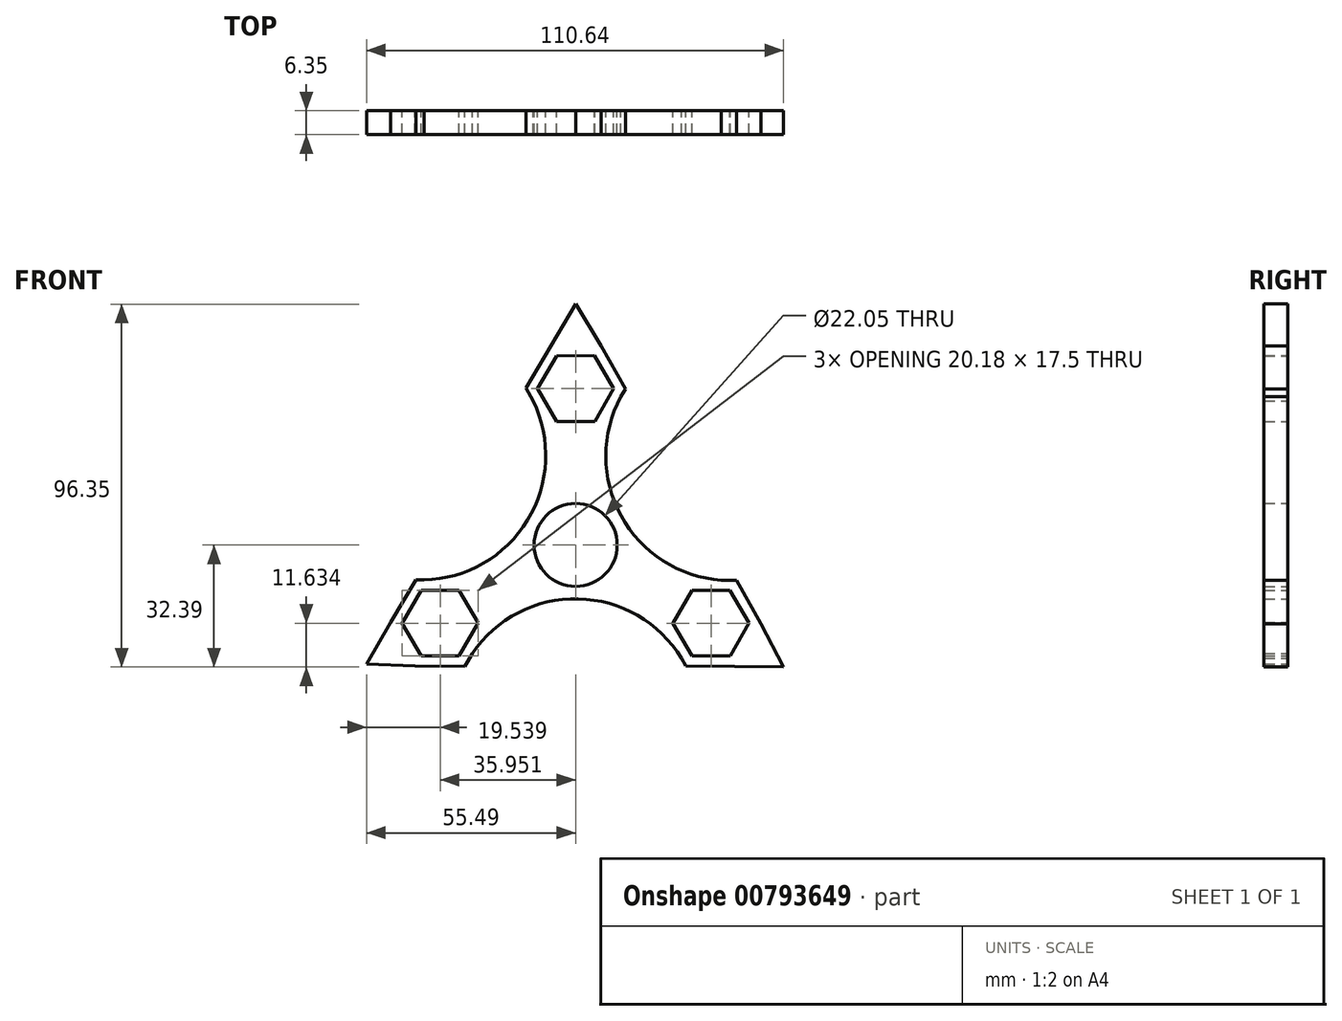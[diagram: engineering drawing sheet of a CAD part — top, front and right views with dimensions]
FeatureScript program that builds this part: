
annotation { "Feature Type Name" : "Feature", "Feature Type Description" : "" }
export const myFeature = defineFeature(function(context is Context, id is Id, definition is map)
    precondition{}
    {
        {
            var Q0;
            Q0=qCreatedBy(makeId("Front.planeOp"),FACE);
            var sketch = newSketch(context, id + "F0", { "sketchPlane" : qUnion([Q0])});
            skCircle(sketch, "E0", {"center": v(0, 0) * mm, "radius": 11.02 * mm});
            skCircle(sketch, "E1", {"center": v(0, 0) * mm, "radius": 14.29 * mm});
            skCircle(sketch, "E2.cCircle", {"center": v(0, 41.51) * mm, "radius": 8.74 * mm, "construction": true});
            skLineSegment(sketch, "E2.0", {"start": v(-10.09, 41.49) * mm, "end": v(-5.06, 50.24) * mm});
            skLineSegment(sketch, "E2.1", {"start": v(-5.06, 50.24) * mm, "end": v(5.02, 50.26) * mm});
            skLineSegment(sketch, "E2.2", {"start": v(5.02, 50.26) * mm, "end": v(10.09, 41.54) * mm});
            skLineSegment(sketch, "E2.3", {"start": v(10.09, 41.54) * mm, "end": v(5.06, 32.79) * mm});
            skLineSegment(sketch, "E2.4", {"start": v(5.06, 32.79) * mm, "end": v(-5.02, 32.76) * mm});
            skLineSegment(sketch, "E2.5", {"start": v(-5.02, 32.76) * mm, "end": v(-10.09, 41.49) * mm});
            skPoint(sketch, "E2.0.midPoint", {"position": v(-7.58, 45.86) * mm});
            skCircle(sketch, "E3.cCircle", {"center": v(0, 41.51) * mm, "radius": 11.43 * mm, "construction": true});
            skLineSegment(sketch, "E3.0", {"start": v(6.72, 52.87) * mm, "end": v(13.2, 41.37) * mm});
            skLineSegment(sketch, "E3.1", {"start": v(13.2, 41.37) * mm, "end": v(6.48, 30.01) * mm});
            skLineSegment(sketch, "E3.2", {"start": v(6.48, 30.01) * mm, "end": v(-6.72, 30.15) * mm});
            skLineSegment(sketch, "E3.3", {"start": v(-6.72, 30.15) * mm, "end": v(-13.2, 41.65) * mm});
            skLineSegment(sketch, "E3.4", {"start": v(-13.2, 41.65) * mm, "end": v(-6.48, 53.01) * mm});
            skLineSegment(sketch, "E3.5", {"start": v(-6.48, 53.01) * mm, "end": v(6.72, 52.87) * mm});
            skPoint(sketch, "E3.0.midPoint", {"position": v(9.96, 47.12) * mm});
            skPoint(sketch, "E4.0.midPoint", {"position": v(6.87, -13.76) * mm});
            skCircle(sketch, "E5.1.0", {"center": v(-35.95, -20.76) * mm, "radius": 8.74 * mm, "construction": true});
            skLineSegment(sketch, "E5.1.1", {"start": v(-22.75, -20.9) * mm, "end": v(-29.47, -32.26) * mm});
            skLineSegment(sketch, "E5.1.2", {"start": v(-29.47, -32.26) * mm, "end": v(-42.67, -32.12) * mm});
            skLineSegment(sketch, "E5.1.3", {"start": v(-42.67, -32.12) * mm, "end": v(-49.15, -20.62) * mm});
            skLineSegment(sketch, "E5.1.4", {"start": v(-49.15, -20.62) * mm, "end": v(-42.43, -9.26) * mm});
            skLineSegment(sketch, "E5.1.5", {"start": v(-42.43, -9.26) * mm, "end": v(-29.23, -9.4) * mm});
            skLineSegment(sketch, "E5.1.6", {"start": v(-29.23, -9.4) * mm, "end": v(-22.75, -20.9) * mm});
            skLineSegment(sketch, "E5.1.7", {"start": v(-30.93, -12) * mm, "end": v(-25.86, -20.73) * mm});
            skLineSegment(sketch, "E5.1.8", {"start": v(-25.86, -20.73) * mm, "end": v(-30.89, -29.48) * mm});
            skLineSegment(sketch, "E5.1.9", {"start": v(-30.89, -29.48) * mm, "end": v(-40.98, -29.5) * mm});
            skLineSegment(sketch, "E5.1.10", {"start": v(-41.02, -12.03) * mm, "end": v(-30.93, -12) * mm});
            skLineSegment(sketch, "E5.1.11", {"start": v(-46.04, -20.78) * mm, "end": v(-41.02, -12.03) * mm});
            skLineSegment(sketch, "E5.1.12", {"start": v(-40.98, -29.5) * mm, "end": v(-46.04, -20.78) * mm});
            skCircle(sketch, "E5.1.13", {"center": v(-35.95, -20.76) * mm, "radius": 11.43 * mm, "construction": true});
            skCircle(sketch, "E5.2.0", {"center": v(35.95, -20.76) * mm, "radius": 8.74 * mm, "construction": true});
            skLineSegment(sketch, "E5.2.1", {"start": v(29.47, -9.26) * mm, "end": v(42.67, -9.4) * mm});
            skLineSegment(sketch, "E5.2.2", {"start": v(42.67, -9.4) * mm, "end": v(49.15, -20.9) * mm});
            skLineSegment(sketch, "E5.2.3", {"start": v(49.15, -20.9) * mm, "end": v(42.43, -32.26) * mm});
            skLineSegment(sketch, "E5.2.4", {"start": v(42.43, -32.26) * mm, "end": v(29.23, -32.12) * mm});
            skLineSegment(sketch, "E5.2.5", {"start": v(29.23, -32.12) * mm, "end": v(22.75, -20.62) * mm});
            skLineSegment(sketch, "E5.2.6", {"start": v(22.75, -20.62) * mm, "end": v(29.47, -9.26) * mm});
            skLineSegment(sketch, "E5.2.7", {"start": v(25.86, -20.78) * mm, "end": v(30.89, -12.03) * mm});
            skLineSegment(sketch, "E5.2.8", {"start": v(30.89, -12.03) * mm, "end": v(40.98, -12) * mm});
            skLineSegment(sketch, "E5.2.9", {"start": v(40.98, -12) * mm, "end": v(46.04, -20.73) * mm});
            skLineSegment(sketch, "E5.2.10", {"start": v(30.93, -29.5) * mm, "end": v(25.86, -20.78) * mm});
            skLineSegment(sketch, "E5.2.11", {"start": v(41.02, -29.48) * mm, "end": v(30.93, -29.5) * mm});
            skLineSegment(sketch, "E5.2.12", {"start": v(46.04, -20.73) * mm, "end": v(41.02, -29.48) * mm});
            skCircle(sketch, "E5.2.13", {"center": v(35.95, -20.76) * mm, "radius": 11.43 * mm, "construction": true});
            skArc(sketch, "E6", {"start": v(-42.43, -9.26) * mm, "mid": v(-12.33, 7.3) * mm, "end": v(-13.2, 41.65) * mm});
            skArc(sketch, "E7", {"start": v(29.23, -32.12) * mm, "mid": v(-0.16, -14.29) * mm, "end": v(-29.47, -32.26) * mm});
            skArc(sketch, "E8", {"start": v(13.2, 41.37) * mm, "mid": v(12.46, 7) * mm, "end": v(42.67, -9.4) * mm});
            skLineSegment(sketch, "E9", {"start": v(-49.15, -20.62) * mm, "end": v(-55.49, -31.66) * mm});
            skLineSegment(sketch, "E10", {"start": v(-55.49, -31.66) * mm, "end": v(-42.67, -32.12) * mm});
            skLineSegment(sketch, "E11", {"start": v(42.43, -32.26) * mm, "end": v(55.15, -32.39) * mm});
            skLineSegment(sketch, "E12", {"start": v(55.15, -32.39) * mm, "end": v(49.15, -20.9) * mm});
            skLineSegment(sketch, "E13", {"start": v(-6.48, 53.01) * mm, "end": v(0, 63.96) * mm});
            skLineSegment(sketch, "E14", {"start": v(0, 63.96) * mm, "end": v(6.72, 52.87) * mm});
            skSolve(sketch);
        }
        {
            var Q0;
            Q0 = qSketchRegion(id + "F0", true);
            var Q1;
            Q1=makeQuery(id+"F0.imprint","IMPRINT",FACE,{"disambiguationData":[TD([[makeQuery(id+"F0.imprint","IMPRINT",EDGE,{"derivedFrom":sQuery(id+"F0.wireOp",EDGE,"E0")}),-1.0]])]});
            extrude(context, id + "F1", {"entities" : qUnion([Q0, Q1]), "depth" : 6.35 * mm, "offsetDistance" : 25.4 * mm});
        }
    });
